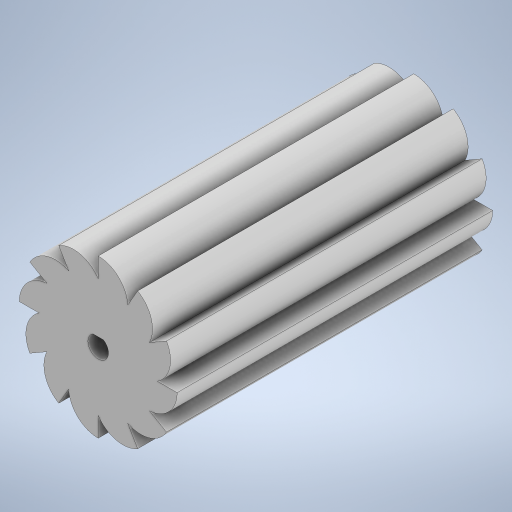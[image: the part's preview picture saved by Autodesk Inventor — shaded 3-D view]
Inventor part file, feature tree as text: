
AUTODESK INVENTOR PART (.ipt)
format: ipt  version: 2023 (Build 270158000, 158)  size: 317,440 bytes
history: native  units: in
note: dims shown in document units (in); Inventor stores cm internally (conversion verified against a paired STEP export)
features: sketch x1, extrude x1
ambient origin geometry x8: Origin, YZ Plane, XZ Plane, XY Plane, X Axis, Y Axis, Z Axis, Center Point
bodies: Solid1 (feature_tree)
feature tree (2):
  sketch  "Sketch1"  dims[d0=2.0in d1=1.5in d11=0.26in d12=4.0in d13=0.0in d17=30.0deg d18=4.7244in d20=360.0deg d27=0.13in]
  extrude  "Extrusion1"  Depth=0.13in
